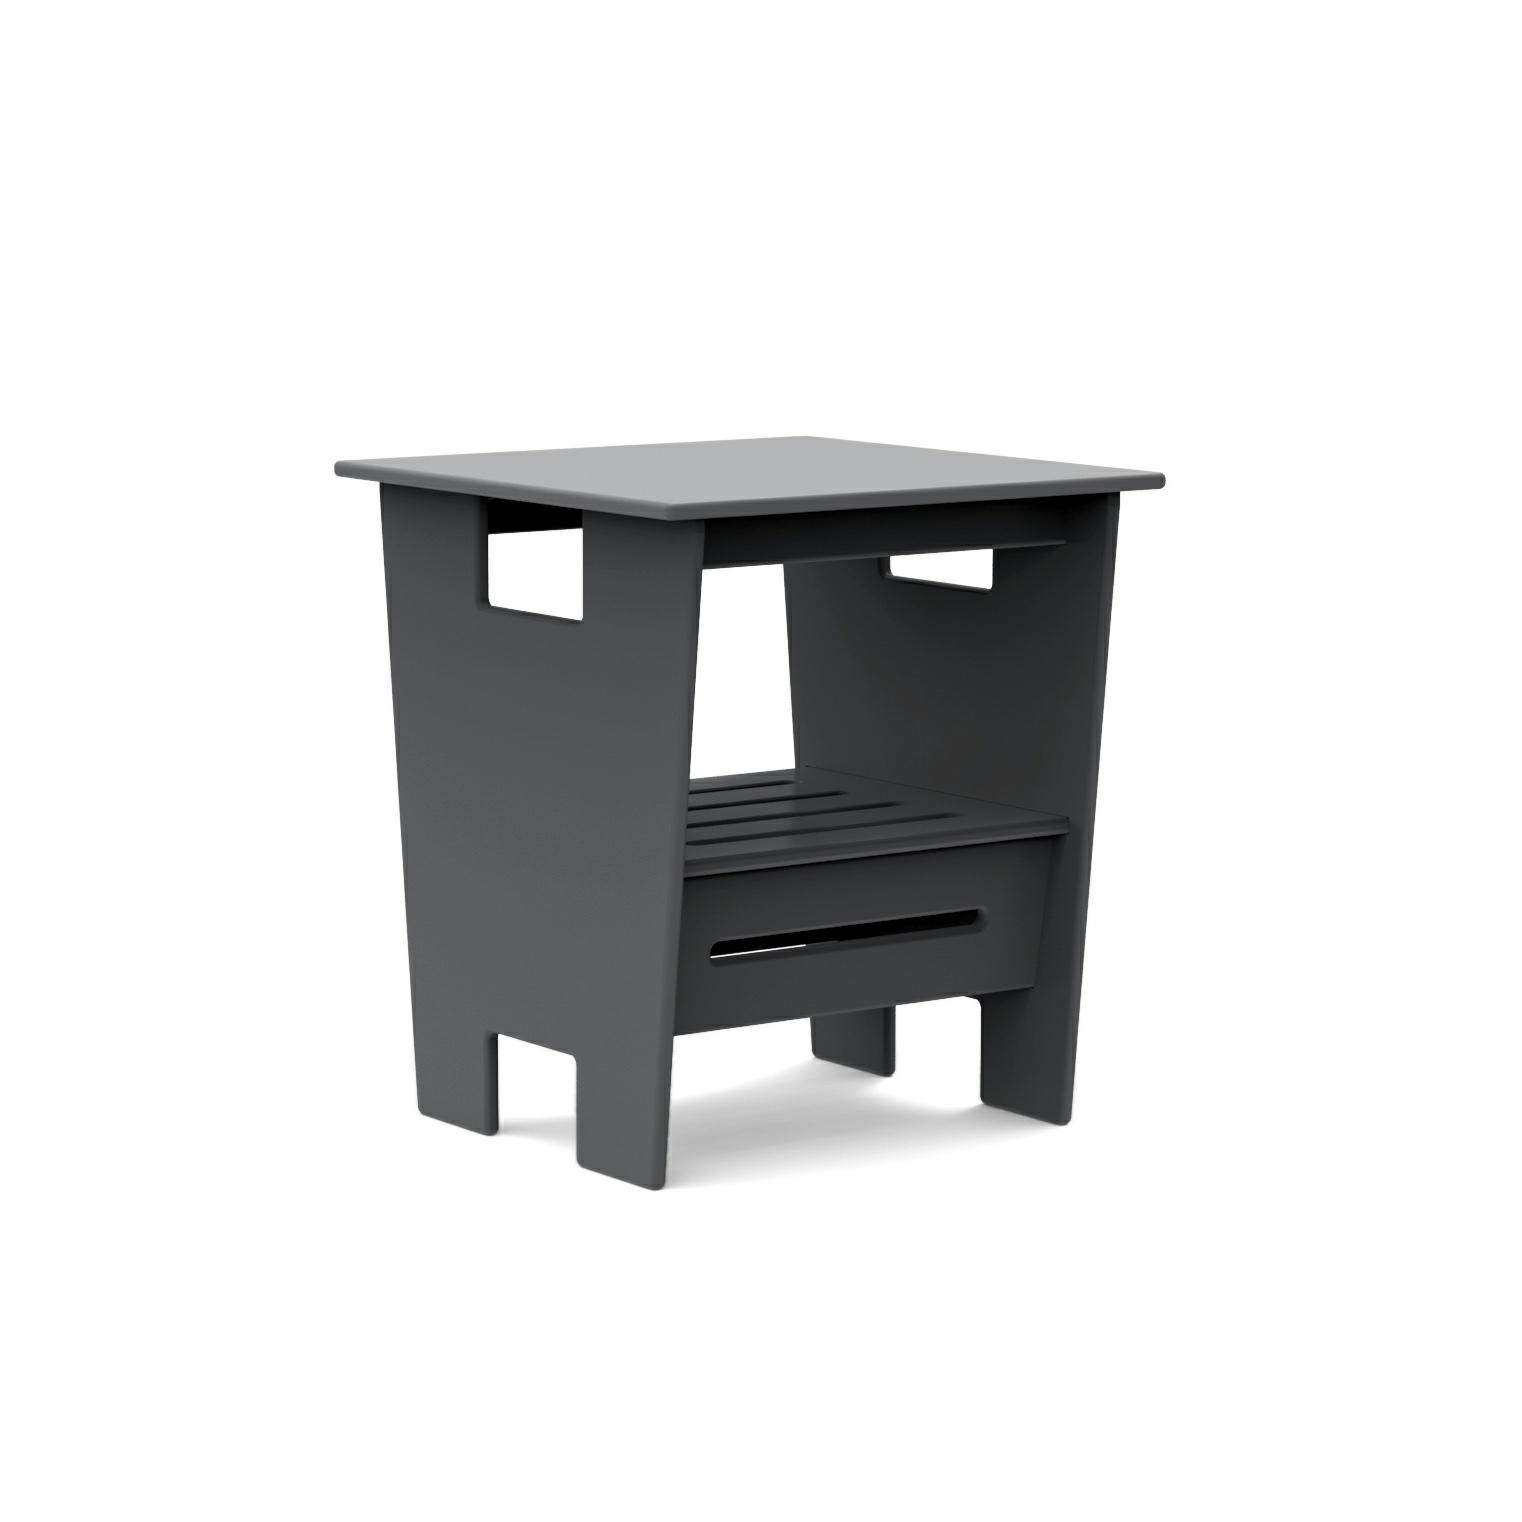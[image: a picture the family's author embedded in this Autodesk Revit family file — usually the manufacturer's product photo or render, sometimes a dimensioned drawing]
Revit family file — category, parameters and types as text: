
# Revit family: Lollygagger Go Side Table
name_source: partatom
category: Furniture
revit_build: Autodesk Revit 2016 (Build: 20150220_1215(x64)
units: mm (PartAtom-declared; Revit-internal decimal feet)

## family parameters
Always vertical = Yes
Cut with Voids When Loaded = No
OmniClass Number = 23.40.20.00
OmniClass Title = General Furniture and Specialties
Room Calculation Point = No
Shared = No
Work Plane-Based = No

## types (11) — shared parameters
Apron = 1' - 6"
Height Top = 1' - 10"
Length = 1' - 7 1/4"
Manufacturer = Loll
Thick = 0' - 1"
Type Image = go_side table.jpg
URL = https://lolldesigns.com
Width = 1' - 7 1/4"

## type names (no varying parameters)
- Loll-Black
- Loll-Sunset
- Loll-Chocolate
- Loll-Sky
- Loll-Apple
- Loll-Leaf
- Loll-Evergreen
- Loll-Charcoal
- Loll-Sand
- Loll-Navy Blue
- Loll-White

note: column(s) folded — value = type name in every type: Finish Material

## geometry (parser evidence)
native form markers: Sweep x1
no freeform markers — native parametric forms only
